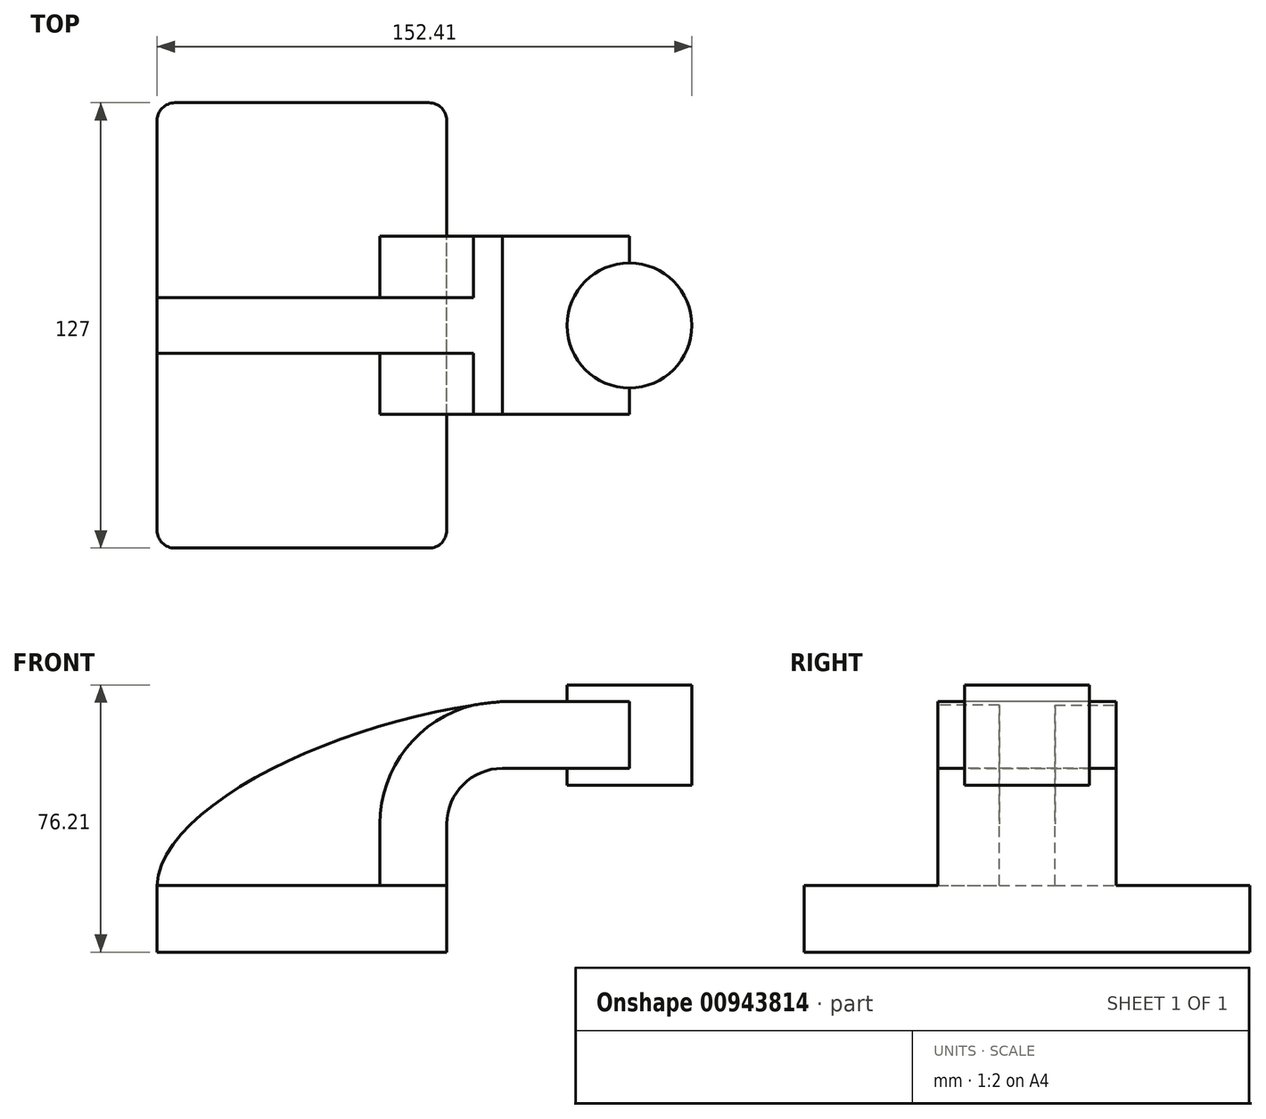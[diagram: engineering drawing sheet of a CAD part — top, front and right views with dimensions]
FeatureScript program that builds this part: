
annotation { "Feature Type Name" : "Feature", "Feature Type Description" : "" }
export const myFeature = defineFeature(function(context is Context, id is Id, definition is map)
    precondition{}
    {
        {
            var Q0;
            Q0=qCreatedBy(makeId("Front.planeOp"),FACE);
            var sketch = newSketch(context, id + "F0", { "sketchPlane" : qUnion([Q0])});
            skLineSegment(sketch, "E0.bottom", {"start": v(41.28, -9.52) * mm, "end": v(-41.28, -9.53) * mm});
            skLineSegment(sketch, "E0.top", {"start": v(41.28, 9.53) * mm, "end": v(-41.28, 9.53) * mm});
            skLineSegment(sketch, "E0.left", {"start": v(41.28, -9.52) * mm, "end": v(41.28, 9.53) * mm});
            skLineSegment(sketch, "E0.right", {"start": v(-41.27, -9.53) * mm, "end": v(-41.28, 9.53) * mm});
            skPoint(sketch, "E0.middle", {"position": v(0, 0) * mm});
            skLineSegment(sketch, "E1.bottom", {"start": v(60.32, 66.68) * mm, "end": v(111.12, 66.68) * mm});
            skLineSegment(sketch, "E1.top", {"start": v(60.32, 38.1) * mm, "end": v(111.12, 38.1) * mm});
            skLineSegment(sketch, "E1.left", {"start": v(60.32, 66.68) * mm, "end": v(60.32, 38.1) * mm});
            skLineSegment(sketch, "E1.right", {"start": v(111.12, 66.68) * mm, "end": v(111.12, 38.1) * mm});
            skLineSegment(sketch, "E2", {"start": v(41.27, 9.53) * mm, "end": v(41.27, 27) * mm});
            skArc(sketch, "E3", {"start": v(41.27, 27) * mm, "mid": v(45.92, 38.23) * mm, "end": v(57.15, 42.88) * mm});
            skLineSegment(sketch, "E4", {"start": v(57.15, 42.88) * mm, "end": v(93.32, 42.88) * mm});
            skArc(sketch, "E5.0", {"start": v(22.22, 27) * mm, "mid": v(32.45, 51.7) * mm, "end": v(57.15, 61.93) * mm});
            skLineSegment(sketch, "E5.1", {"start": v(22.22, 9.53) * mm, "end": v(22.22, 27) * mm});
            skLineSegment(sketch, "E6", {"start": v(57.15, 61.93) * mm, "end": v(93.32, 61.93) * mm});
            skLineSegment(sketch, "E7", {"start": v(93.32, 38.1) * mm, "end": v(93.32, 66.68) * mm});
            skFitSpline(sketch, "E8", {"points": [v(-41.28, 9.53) * mm, v(57.15, 61.93) * mm], "startDerivative": vector(3.04, 71.69) * mm, "endDerivative": vector(126.59, 11.5) * mm});
            skSolve(sketch);
        }
        {
            var Q0;
            Q0=makeQuery(id+"F0.imprint","IMPRINT",FACE,{"disambiguationData":[TD([[makeQuery(id+"F0.imprint","IMPRINT",EDGE,{"derivedFrom":sQuery(id+"F0.wireOp",EDGE,"E0.bottom")}),-1.0]])]});
            extrude(context, id + "F1", {"entities" : qUnion([Q0]), "endBound" : BoundingType.SYMMETRIC, "depth" : 127 * mm, "offsetDistance" : 25.4 * mm});
        }
        {
            var Q0;
            {var subQ0=sQuery(id+"F0.wireOp",EDGE,"E6");var subQ1=sQuery(id+"F0.wireOp",EDGE,"E1.left");var subQ2=makeQuery(id+"F0.imprint","INTERSECT",VERTEX,{"derivedFrom":[subQ1,subQ0]});Q0=makeQuery(id+"F0.imprint","IMPRINT",FACE,{"disambiguationData":[TD([[makeQuery(id+"F0.imprint","IMPRINT",EDGE,{"disambiguationData":[TD([[subQ2,-1.0]])],"derivedFrom":subQ1}),1.0]])]});}
            var Q1;
            {var subQ1=sQuery(id+"F0.wireOp",EDGE,"E2");Q1=makeQuery(id+"F0.imprint","IMPRINT",FACE,{"disambiguationData":[TD([[makeQuery(id+"F0.imprint","IMPRINT",EDGE,{"derivedFrom":subQ1}),1.0]])]});}
            extrude(context, id + "F2", {"entities" : qUnion([Q0, Q1]), "operationType" : NewBodyOperationType.ADD, "endBound" : BoundingType.SYMMETRIC, "depth" : 50.8 * mm, "offsetDistance" : 25.4 * mm});
        }
        {
            var Q0;
            {var subQ3=sQuery(id+"F0.wireOp",EDGE,"E5.1");Q0=makeQuery(id+"F0.imprint","IMPRINT",FACE,{"disambiguationData":[TD([[makeQuery(id+"F0.imprint","IMPRINT",EDGE,{"derivedFrom":subQ3}),1.0]])]});}
            extrude(context, id + "F3", {"entities" : qUnion([Q0]), "operationType" : NewBodyOperationType.ADD, "endBound" : BoundingType.SYMMETRIC, "depth" : 15.88 * mm, "offsetDistance" : 25.4 * mm});
        }
        {
            var Q0;
            {var subQ4=sQuery(id+"F0.wireOp",EDGE,"E1.right");Q0=makeQuery(id+"F0.imprint","IMPRINT",FACE,{"disambiguationData":[TD([[makeQuery(id+"F0.imprint","IMPRINT",EDGE,{"derivedFrom":subQ4}),-1.0]])]});}
            var Q1;
            Q1=sQuery(id+"F0.wireOp",EDGE,"E7");
            revolve(context, id + "F4", {"operationType" : NewBodyOperationType.ADD, "surfaceOperationType" : NewSurfaceOperationType.NEW, "entities" : qUnion([Q0]), "axis" : qUnion([Q1]), "revolveType" : RevolveType.FULL});
        }
        {
            var Q0;
            Q0=makeQuery(id+"F1.opExtrude","CAP_EDGE",EDGE,{"disambiguationData":[OSD([sQuery(id+"F0.wireOp",EDGE,"E0.right")])],"isStart":false});
            var Q1;
            Q1=makeQuery(id+"F1.opExtrude","CAP_EDGE",EDGE,{"disambiguationData":[OSD([sQuery(id+"F0.wireOp",EDGE,"E0.left")])],"isStart":false});
            var Q2;
            Q2=makeQuery(id+"F1.opExtrude","CAP_EDGE",EDGE,{"disambiguationData":[OSD([sQuery(id+"F0.wireOp",EDGE,"E0.right")])],"isStart":true});
            var Q3;
            Q3=makeQuery(id+"F1.opExtrude","CAP_EDGE",EDGE,{"disambiguationData":[OSD([sQuery(id+"F0.wireOp",EDGE,"E0.left")])],"isStart":true});
            fillet(context, id + "F5", {"entities" : qUnion([Q0, Q1, Q2, Q3]), "radius" : 5.08 * mm, "tangentPropagation" : true, "allowEdgeOverflow" : false});
        }
    });
